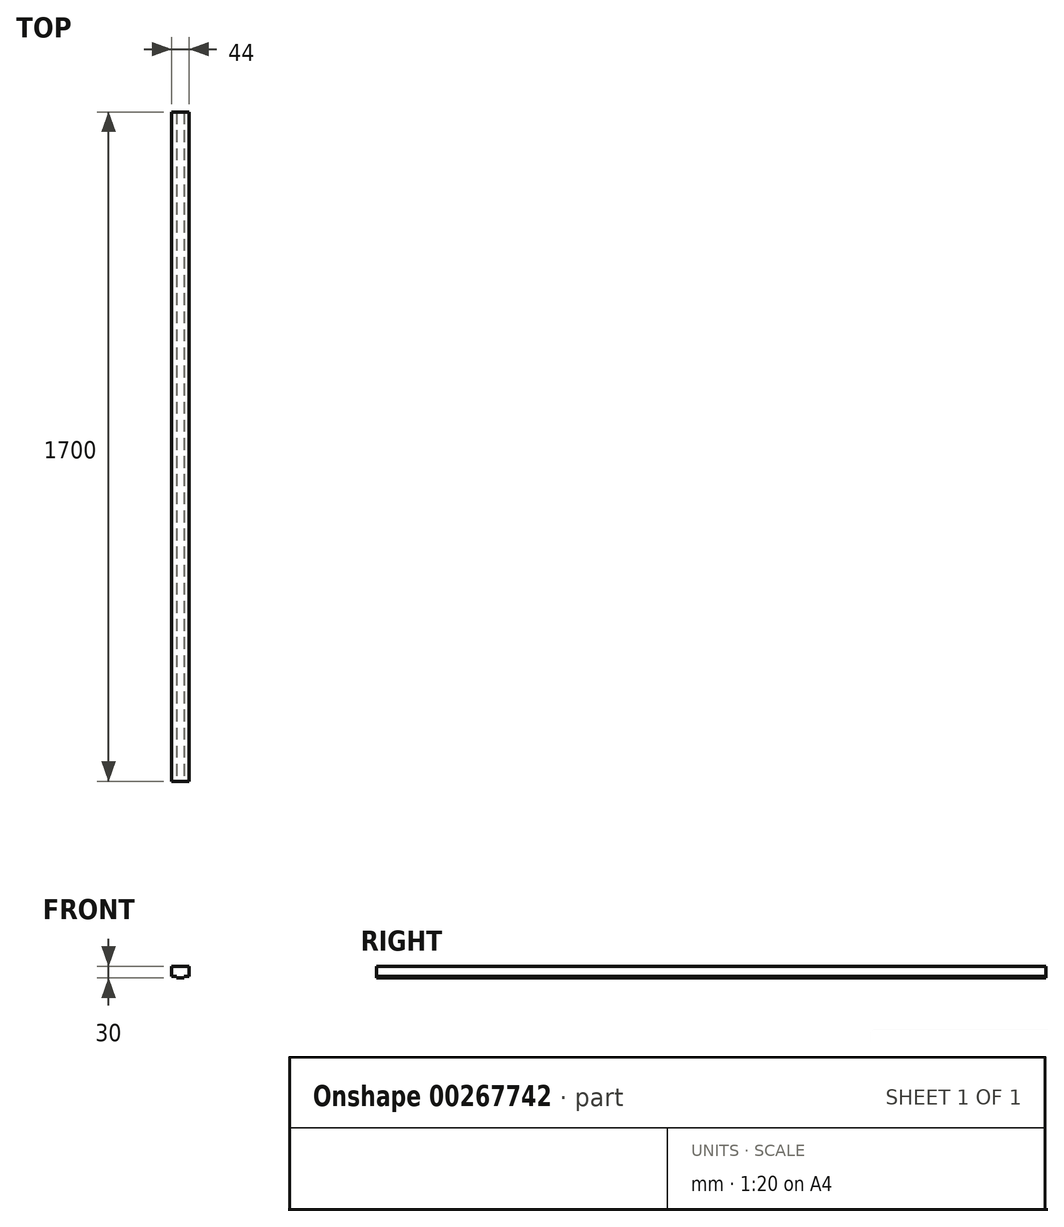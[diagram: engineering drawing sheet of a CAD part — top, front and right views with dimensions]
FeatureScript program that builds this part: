
annotation { "Feature Type Name" : "Feature", "Feature Type Description" : "" }
export const myFeature = defineFeature(function(context is Context, id is Id, definition is map)
    precondition{}
    {
        {
            var Q0;
            Q0=qCreatedBy(makeId("Front.planeOp"),FACE);
            var sketch = newSketch(context, id + "F0", { "sketchPlane" : qUnion([Q0])});
            skLineSegment(sketch, "E0.bottom", {"start": v(10, -15) * mm, "end": v(-10, -15) * mm});
            skLineSegment(sketch, "E0.top", {"start": v(22, 15) * mm, "end": v(-22, 15) * mm});
            skLineSegment(sketch, "E0.left", {"start": v(22, -10.4) * mm, "end": v(22, 15) * mm});
            skLineSegment(sketch, "E0.right", {"start": v(-22, -10.4) * mm, "end": v(-22, 15) * mm});
            skPoint(sketch, "E0.middle", {"position": v(0, 0) * mm});
            skLineSegment(sketch, "E1", {"start": v(0, -23.3) * mm, "end": v(-10, -23.3) * mm, "construction": true});
            skLineSegment(sketch, "E2", {"start": v(-10, -23.3) * mm, "end": v(-10, 2.5) * mm, "construction": true});
            skLineSegment(sketch, "E3", {"start": v(-10, 2.5) * mm, "end": v(10, 2.5) * mm, "construction": true});
            skLineSegment(sketch, "E4", {"start": v(10, 2.5) * mm, "end": v(10, -15) * mm, "construction": true});
            skLineSegment(sketch, "E5", {"start": v(-10, -15) * mm, "end": v(-10, -10.4) * mm});
            skLineSegment(sketch, "E6", {"start": v(-10, -10.4) * mm, "end": v(-22, -10.4) * mm});
            skLineSegment(sketch, "E7", {"start": v(10, -10.4) * mm, "end": v(22, -10.4) * mm});
            skLineSegment(sketch, "E8", {"start": v(10, -10.4) * mm, "end": v(10, -15) * mm});
            skPoint(sketch, "E9", {"position": v(0, 15) * mm});
            skSolve(sketch);
        }
        {
            var Q0;
            Q0=qSketchRegion(id+"F0",true);
            extrude(context, id + "F1", {"entities" : qUnion([Q0]), "oppositeDirection" : true, "depth" : 1700 * mm});
        }
    });
